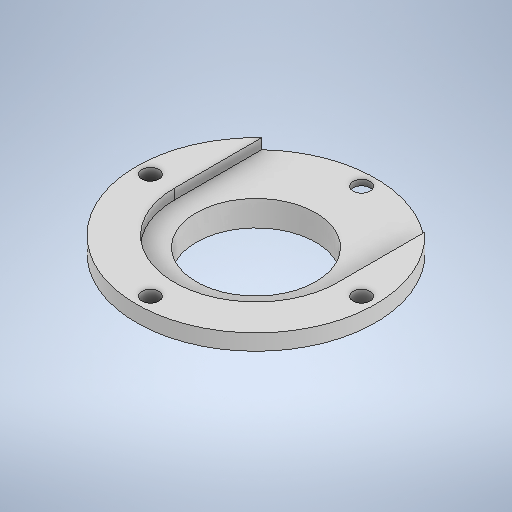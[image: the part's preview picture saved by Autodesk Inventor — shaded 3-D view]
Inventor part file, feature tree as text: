
AUTODESK INVENTOR PART (.ipt)
format: ipt  version: 2025.2 (Build 292293000, 293)  size: 272,896 bytes
history: native  units: mm
features: sketch x5, extrude x4
ambient origin geometry x8: Origin, YZ Plane, XZ Plane, XY Plane, X Axis, Y Axis, Z Axis, Center Point
bodies: Solid1 (feature_tree)
feature tree (9):
  extrude  "Extrusion1"  Depth=45.0mm
  extrude  "Extrusion2"  Depth=4.3mm
  extrude  "Extrusion3"  Depth=4.0mm TaperAngle=0.0deg
  extrude  "Extrusion4"  Depth=2.6mm TaperAngle=0.0deg
  sketch  "Sketch1"  dims[d0=60.0mm d1=45.0mm]
  sketch  "Sketch Circular Pattern1"  dims[d3=53.0mm d4=4.3mm]
  sketch  "Sketch2"  dims[d5=40.0mm d7=360.0deg d9=4.0mm d10=0.0mm]
  sketch  "Sketch3"  dims[d11=41.0mm d12=2.6mm d13=0.0mm]
  sketch  "Sketch4"  dims[d14=30.0mm d15=0.0mm d16=0.0mm d17=30.0mm d18=35.0mm d19=5.0mm d20=0.0mm]
